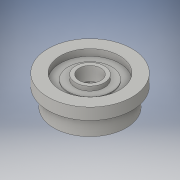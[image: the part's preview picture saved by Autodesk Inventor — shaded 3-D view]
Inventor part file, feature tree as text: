
AUTODESK INVENTOR PART (.ipt)
format: ipt  version: 2016 (Build 200138000, 138)  size: 146,432 bytes
history: native  units: in
note: dims shown in document units (in); Inventor stores cm internally (conversion verified against a paired STEP export)
features: extrude x7, sketch x7
ambient origin geometry x8: Origin, YZ Plane, XZ Plane, XY Plane, X Axis, Y Axis, Z Axis, Center Point
bodies: Solid1 (feature_tree)
feature tree (14):
  extrude  "Extrusion1"  Depth=0.6299in TaperAngle=0.0deg
  extrude  "Extrusion2"  Depth=0.3543in TaperAngle=0.0deg
  extrude  "Extrusion3"  Depth=0.9843in TaperAngle=0.0deg
  extrude  "Extrusion4"  Depth=0.0512in TaperAngle=0.0deg
  extrude  "Extrusion5"  Depth=0.2362in TaperAngle=0.0deg
  extrude  "Extrusion6"  Depth=1.9685in TaperAngle=0.0deg
  extrude  "Extrusion7"  [1 undecoded]
  sketch  "Sketch1"  dims[d0=4.5669in d1=0.6299in d2=0.0in]
  sketch  "Sketch2"  dims[d3=3.2283in d4=0.3543in d5=0.0in]
  sketch  "Sketch3"  dims[d6=3.937in d7=0.9843in d8=0.0in]
  sketch  "Sketch4"  dims[d9=2.3622in d10=0.0512in d11=0.0in]
  sketch  "Sketch6"  dims[d12=1.5748in d13=0.2362in d14=0.0in]
  sketch  "Sketch7"  dims[d15=1.1811in d16=1.9685in d17=0.0in]
  sketch  "Sketch8"  dims[d18=0.7874in d19=0.0in]
note: 1 required parameter value undecoded (feature->parameter linkage not recoverable at this tier; creation-order binding heuristic only, values carry confidence <= 0.55)
